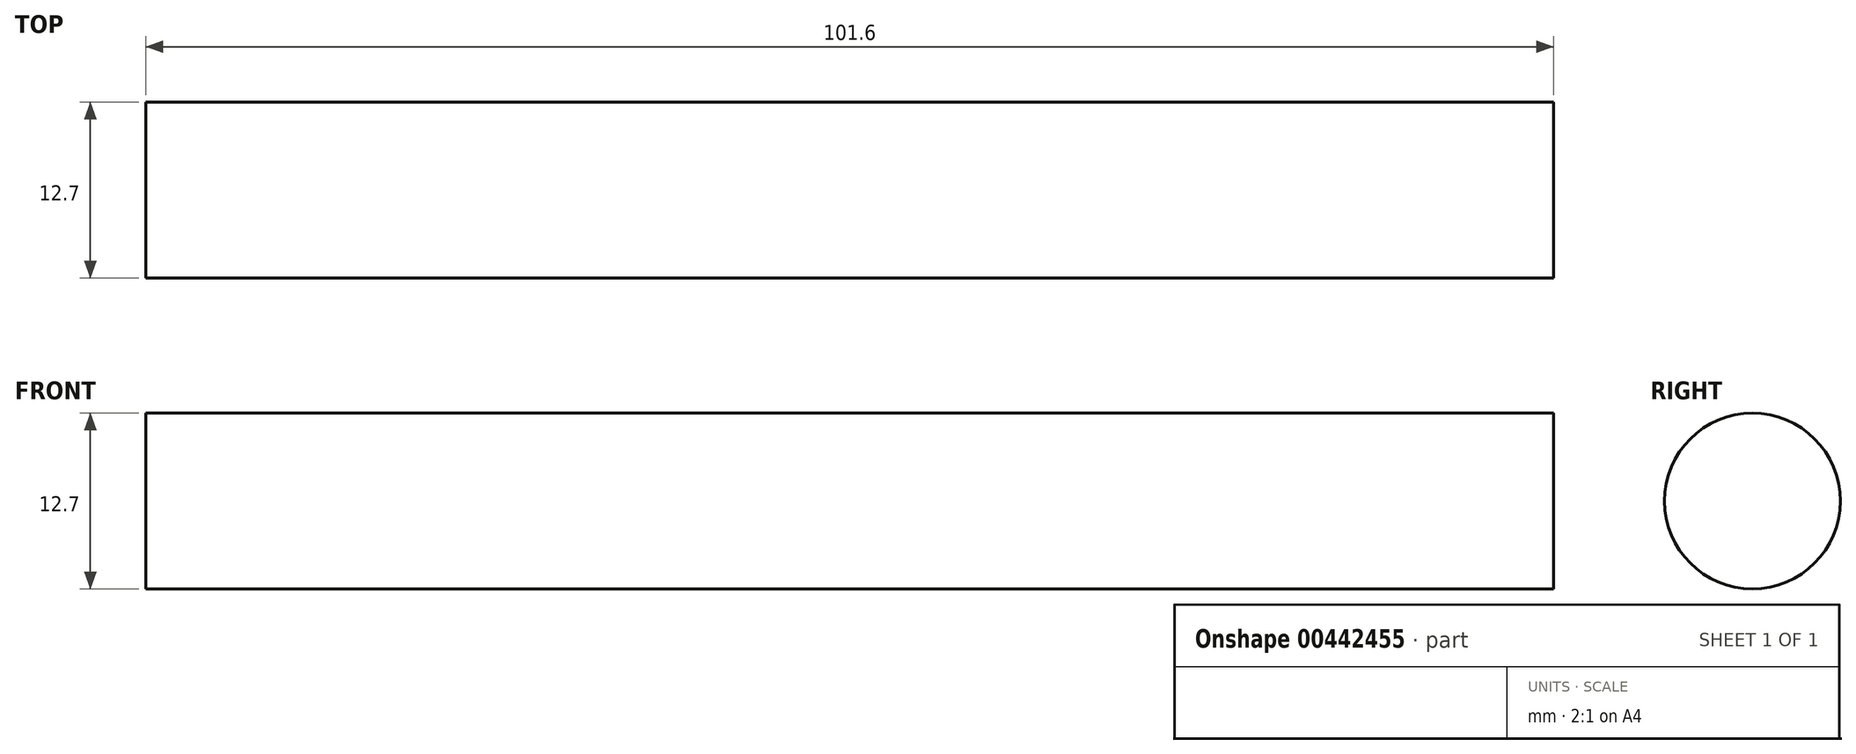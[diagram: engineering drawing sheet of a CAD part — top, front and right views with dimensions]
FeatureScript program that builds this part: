
annotation { "Feature Type Name" : "Feature", "Feature Type Description" : "" }
export const myFeature = defineFeature(function(context is Context, id is Id, definition is map)
    precondition{}
    {
        {
            var Q0;
            Q0=qCreatedBy(makeId("Right.planeOp"),FACE);
            var sketch = newSketch(context, id + "F0", { "sketchPlane" : qUnion([Q0])});
            skCircle(sketch, "E0", {"center": v(0, 0) * mm, "radius": 6.35 * mm});
            skSolve(sketch);
        }
        {
            var Q0;
            Q0 = qSketchRegion(id + "F0", true);
            extrude(context, id + "F1", {"entities" : qUnion([Q0]), "depth" : 50.8 * mm, "hasSecondDirection" : true, "secondDirectionOppositeDirection" : true, "secondDirectionDepth" : 50.8 * mm});
        }
    });
